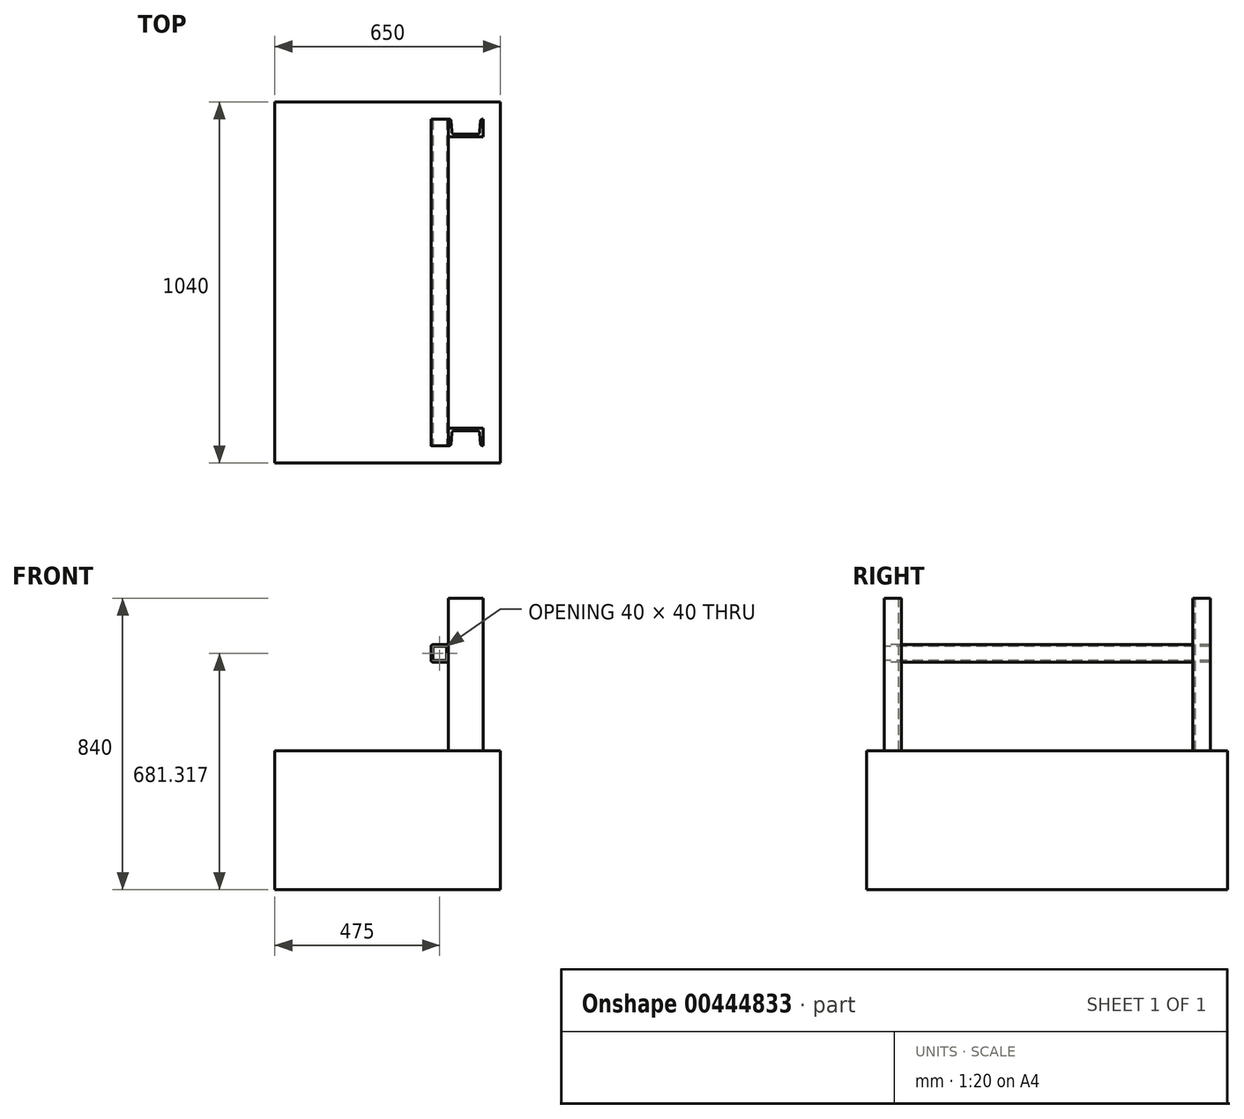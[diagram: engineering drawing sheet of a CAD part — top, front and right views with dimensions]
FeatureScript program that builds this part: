
annotation { "Feature Type Name" : "Feature", "Feature Type Description" : "" }
export const myFeature = defineFeature(function(context is Context, id is Id, definition is map)
    precondition{}
    {
        {
            var Q0;
            Q0=qCreatedBy(makeId("Top.planeOp"),FACE);
            var sketch = newSketch(context, id + "F0", { "sketchPlane" : qUnion([Q0])});
            skLineSegment(sketch, "E0.bottom", {"start": v(-60, -22.5) * mm, "end": v(40, -22.5) * mm});
            skLineSegment(sketch, "E0.top", {"start": v(-60, 27.5) * mm, "end": v(-53.2, 27.5) * mm});
            skLineSegment(sketch, "E0.left", {"start": v(-60, -22.5) * mm, "end": v(-60, 27.5) * mm});
            skLineSegment(sketch, "E0.right", {"start": v(40, -22.5) * mm, "end": v(40, 27.5) * mm});
            skLineSegment(sketch, "E1.0", {"start": v(-49.76, -15.5) * mm, "end": v(29.76, -15.5) * mm});
            skLineSegment(sketch, "E2.trimOffspring", {"start": v(33.2, 27.5) * mm, "end": v(40, 27.5) * mm});
            skLineSegment(sketch, "E3", {"start": v(-53.2, 27.5) * mm, "end": v(-49.76, -15.5) * mm});
            skLineSegment(sketch, "E4", {"start": v(33.2, 27.5) * mm, "end": v(29.76, -15.5) * mm});
            skPoint(sketch, "E5", {"position": v(-51, 0) * mm});
            skPoint(sketch, "E6", {"position": v(31, 0) * mm});
            skPoint(sketch, "E7", {"position": v(-10, -15.5) * mm});
            skSolve(sketch);
        }
        {
            var Q0;
            Q0=makeQuery(id+"F0.imprint","IMPRINT",FACE,{"disambiguationData":[TD([[makeQuery(id+"F0.imprint","IMPRINT",EDGE,{"derivedFrom":sQuery(id+"F0.wireOp",EDGE,"E0.bottom")}),1.0]])]});
            extrude(context, id + "F1", {"entities" : qUnion([Q0]), "oppositeDirection" : true, "depth" : 440 * mm});
        }
        {
            var Q0;
            Q0=makeQuery(id+"F1.opExtrude","SWEPT_EDGE",EDGE,{"disambiguationData":[OSD([sQuery(id+"F0.wireOp",EDGE,"E0.top"),sQuery(id+"F0.wireOp",EDGE,"E3")])]});
            var Q1;
            Q1=makeQuery(id+"F1.opExtrude","SWEPT_EDGE",EDGE,{"disambiguationData":[OSD([sQuery(id+"F0.wireOp",EDGE,"E2.trimOffspring"),sQuery(id+"F0.wireOp",EDGE,"E4")])]});
            fillet(context, id + "F2", {"entities" : qUnion([Q0, Q1]), "radius" : 4 * mm, "tangentPropagation" : true, "allowEdgeOverflow" : false});
        }
        {
            var Q0;
            Q0=makeQuery(id+"F1.opExtrude","SWEPT_EDGE",EDGE,{"disambiguationData":[OSD([sQuery(id+"F0.wireOp",EDGE,"E1.0"),sQuery(id+"F0.wireOp",EDGE,"E3")])]});
            var Q1;
            Q1=makeQuery(id+"F1.opExtrude","SWEPT_EDGE",EDGE,{"disambiguationData":[OSD([sQuery(id+"F0.wireOp",EDGE,"E1.0"),sQuery(id+"F0.wireOp",EDGE,"E4")])]});
            fillet(context, id + "F3", {"entities" : qUnion([Q0, Q1]), "radius" : 8 * mm, "tangentPropagation" : true, "allowEdgeOverflow" : false});
        }
        {
            var Q0;
            Q0=makeQuery(id+"F1.opExtrude","SWEPT_FACE",FACE,{"disambiguationData":[OSD([sQuery(id+"F0.wireOp",EDGE,"E0.bottom")])]});
            cPlane(context, id + "F4", {"entities" : qUnion([Q0]), "cplaneType" : CPlaneType.OFFSET, "offset" : 420 * mm, "width" : 150 * mm, "height" : 150 * mm});
        }
        {
            var Q0;
            Q0=makeQuery(id+"F1.opExtrude","SWEPT_BODY",BODY,{"disambiguationData":[OSD([sQuery(id+"F0.wireOp",EDGE,"E0.bottom"),sQuery(id+"F0.wireOp",EDGE,"E0.top"),sQuery(id+"F0.wireOp",EDGE,"E0.left"),sQuery(id+"F0.wireOp",EDGE,"E0.right"),sQuery(id+"F0.wireOp",EDGE,"E1.0"),sQuery(id+"F0.wireOp",EDGE,"E2.trimOffspring"),sQuery(id+"F0.wireOp",EDGE,"E3"),sQuery(id+"F0.wireOp",EDGE,"E4")])]});
            var Q1;
            Q1=qCreatedBy(id+"F4.planeOp",FACE);
            mirror(context, id + "F5", {"entities" : qUnion([Q0]), "mirrorPlane" : qUnion([Q1])});
        }
        {
            var Q0;
            Q0=makeQuery(id+"F1.opExtrude","CAP_FACE",FACE,{"disambiguationData":[OSD([sQuery(id+"F0.wireOp",EDGE,"E0.bottom"),sQuery(id+"F0.wireOp",EDGE,"E0.top"),sQuery(id+"F0.wireOp",EDGE,"E0.left"),sQuery(id+"F0.wireOp",EDGE,"E0.right"),sQuery(id+"F0.wireOp",EDGE,"E1.0"),sQuery(id+"F0.wireOp",EDGE,"E2.trimOffspring"),sQuery(id+"F0.wireOp",EDGE,"E3"),sQuery(id+"F0.wireOp",EDGE,"E4")])],"isStart":false});
            var sketch = newSketch(context, id + "F6", { "sketchPlane" : qUnion([Q0])});
            skLineSegment(sketch, "E8.bottom", {"start": v(-560, -77.5) * mm, "end": v(90, -77.5) * mm});
            skLineSegment(sketch, "E8.top", {"start": v(-560, 962.5) * mm, "end": v(90, 962.5) * mm});
            skLineSegment(sketch, "E8.left", {"start": v(-560, -77.5) * mm, "end": v(-560, 962.5) * mm});
            skLineSegment(sketch, "E8.right", {"start": v(90, -77.5) * mm, "end": v(90, 962.5) * mm});
            skSolve(sketch);
        }
        {
            var Q0;
            Q0 = qSketchRegion(id + "F6", true);
            extrude(context, id + "F7", {"entities" : qUnion([Q0]), "depth" : 400 * mm});
        }
        {
            var Q0;
            Q0=makeQuery(id+"F5.opPattern","COPY",FACE,{"derivedFrom":makeQuery(id+"F1.opExtrude","SWEPT_FACE",FACE,{"disambiguationData":[OSD([sQuery(id+"F0.wireOp",EDGE,"E0.top")])]}),"instanceName":"1"});
            cPlane(context, id + "F8", {"entities" : qUnion([Q0]), "cplaneType" : CPlaneType.OFFSET, "offset" : 0 * mm, "width" : 150 * mm, "height" : 150 * mm});
        }
        {
            var Q0;
            Q0=qCreatedBy(id+"F8.planeOp",FACE);
            var sketch = newSketch(context, id + "F9", { "sketchPlane" : qUnion([Q0])});
            skLineSegment(sketch, "E9.bottom", {"start": v(-65, -133.68) * mm, "end": v(-105, -133.68) * mm});
            skLineSegment(sketch, "E9.top", {"start": v(-65, -183.68) * mm, "end": v(-105, -183.68) * mm});
            skLineSegment(sketch, "E9.left", {"start": v(-60, -138.68) * mm, "end": v(-60, -178.68) * mm});
            skLineSegment(sketch, "E9.right", {"start": v(-110, -138.68) * mm, "end": v(-110, -178.68) * mm});
            skLineSegment(sketch, "E10.bottom", {"start": v(-104, -138.68) * mm, "end": v(-66, -138.68) * mm});
            skLineSegment(sketch, "E10.top", {"start": v(-104, -178.68) * mm, "end": v(-66, -178.68) * mm});
            skLineSegment(sketch, "E10.left", {"start": v(-105, -139.68) * mm, "end": v(-105, -177.68) * mm});
            skLineSegment(sketch, "E10.right", {"start": v(-65, -139.68) * mm, "end": v(-65, -177.68) * mm});
            skPoint(sketch, "E11.visualSharp", {"position": v(-110, -133.68) * mm});
            skArc(sketch, "E11.filletArc", {"start": v(-105, -133.68) * mm, "mid": v(-108.54, -135.15) * mm, "end": v(-110, -138.68) * mm});
            skArc(sketch, "E12.filletArc", {"start": v(-104, -138.68) * mm, "mid": v(-104.7, -138.98) * mm, "end": v(-105, -139.68) * mm});
            skPoint(sketch, "E13.visualSharp", {"position": v(-110, -183.68) * mm});
            skArc(sketch, "E13.filletArc", {"start": v(-110, -178.68) * mm, "mid": v(-108.54, -182.22) * mm, "end": v(-105, -183.68) * mm});
            skPoint(sketch, "E14.visualSharp", {"position": v(-60, -183.68) * mm});
            skArc(sketch, "E14.filletArc", {"start": v(-65, -183.68) * mm, "mid": v(-61.46, -182.22) * mm, "end": v(-60, -178.68) * mm});
            skPoint(sketch, "E15.visualSharp", {"position": v(-60, -133.68) * mm});
            skArc(sketch, "E15.filletArc", {"start": v(-60, -138.68) * mm, "mid": v(-61.46, -135.15) * mm, "end": v(-65, -133.68) * mm});
            skArc(sketch, "E16.filletArc", {"start": v(-65, -139.68) * mm, "mid": v(-65.3, -138.98) * mm, "end": v(-66, -138.68) * mm});
            skArc(sketch, "E17.filletArc", {"start": v(-66, -178.68) * mm, "mid": v(-65.3, -178.39) * mm, "end": v(-65, -177.68) * mm});
            skArc(sketch, "E18.filletArc", {"start": v(-105, -177.68) * mm, "mid": v(-104.7, -178.39) * mm, "end": v(-104, -178.68) * mm});
            skSolve(sketch);
        }
        {
            var Q0;
            Q0 = qSketchRegion(id + "F9", true);
            var Q1;
            Q1=makeQuery(id+"F1.opExtrude","SWEPT_FACE",FACE,{"disambiguationData":[OSD([sQuery(id+"F0.wireOp",EDGE,"E0.top")])]});
            extrude(context, id + "F10", {"entities" : qUnion([Q0]), "oppositeDirection" : true, "endBoundEntityFace" : qUnion([Q1]), "depth" : 940 * mm});
        }
    });
